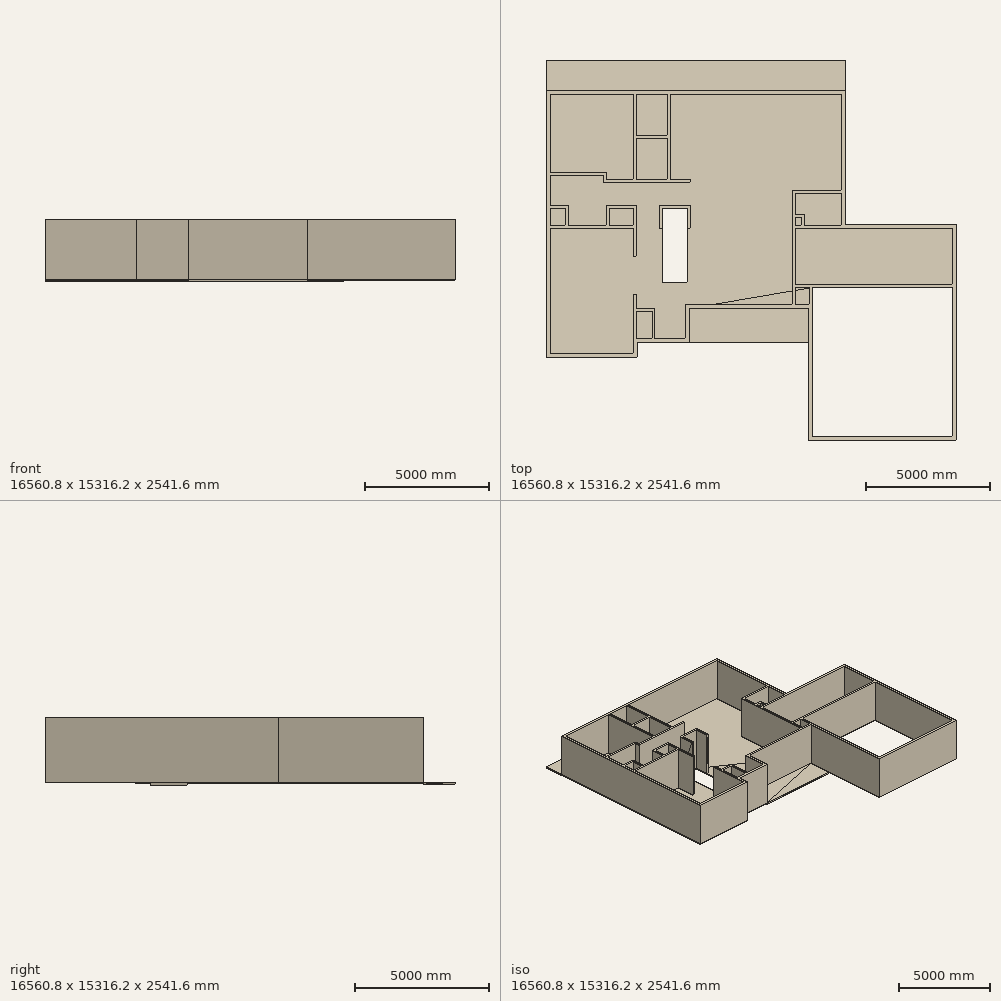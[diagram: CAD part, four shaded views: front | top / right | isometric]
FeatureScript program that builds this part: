
annotation { "Feature Type Name" : "Feature", "Feature Type Description" : "" }
export const myFeature = defineFeature(function(context is Context, id is Id, definition is map)
    precondition{}
    {
        {
            var Q0;
            Q0=qCreatedBy(makeId("Top.planeOp"),FACE);
            cPlane(context, id + "F0", {"entities" : qUnion([Q0]), "cplaneType" : CPlaneType.OFFSET, "offset" : 1.59 * mm, "oppositeDirection" : true, "width" : 152.4 * mm, "height" : 152.4 * mm});
        }
        {
            var Q0;
            Q0=qCreatedBy(makeId("Top.planeOp"),FACE);
            var sketch = newSketch(context, id + "F1", { "sketchPlane" : qUnion([Q0])});
            skLineSegment(sketch, "E0", {"start": v(0, 0) * mm, "end": v(0, 10769.6) * mm});
            skLineSegment(sketch, "E1", {"start": v(0, 10769.6) * mm, "end": v(12065, 10769.6) * mm});
            skLineSegment(sketch, "E2", {"start": v(12065, 10769.6) * mm, "end": v(12065, 5359.4) * mm});
            skLineSegment(sketch, "E3", {"start": v(12065, 5359.4) * mm, "end": v(16560.8, 5359.4) * mm});
            skLineSegment(sketch, "E4", {"start": v(16560.8, 5359.4) * mm, "end": v(16560.8, -3352.8) * mm});
            skLineSegment(sketch, "E5", {"start": v(16560.8, -3352.8) * mm, "end": v(10579.1, -3352.8) * mm});
            skLineSegment(sketch, "E6", {"start": v(10579.1, -3352.8) * mm, "end": v(10579.1, 1955.8) * mm});
            skLineSegment(sketch, "E7", {"start": v(10579.1, 1955.8) * mm, "end": v(5778.5, 1955.8) * mm});
            skLineSegment(sketch, "E8", {"start": v(5778.5, 1955.8) * mm, "end": v(5778.5, 584.2) * mm});
            skLineSegment(sketch, "E9.0", {"start": v(152.4, 152.4) * mm, "end": v(152.4, 10617.2) * mm, "construction": true});
            skLineSegment(sketch, "E9.2", {"start": v(152.4, 10617.2) * mm, "end": v(11912.6, 10617.2) * mm, "construction": true});
            skLineSegment(sketch, "E9.3", {"start": v(5626.1, 2108.2) * mm, "end": v(5626.1, 736.6) * mm, "construction": true});
            skLineSegment(sketch, "E9.4", {"start": v(10731.5, 2108.2) * mm, "end": v(5626.1, 2108.2) * mm, "construction": true});
            skLineSegment(sketch, "E9.5", {"start": v(10731.5, -3200.4) * mm, "end": v(10731.5, 2108.2) * mm, "construction": true});
            skLineSegment(sketch, "E9.6", {"start": v(11912.6, 10617.2) * mm, "end": v(11912.6, 5207) * mm, "construction": true});
            skLineSegment(sketch, "E9.7", {"start": v(11912.6, 5207) * mm, "end": v(16408.4, 5207) * mm, "construction": true});
            skLineSegment(sketch, "E9.8", {"start": v(16408.4, 5207) * mm, "end": v(16408.4, -3200.4) * mm, "construction": true});
            skLineSegment(sketch, "E9.9", {"start": v(16408.4, -3200.4) * mm, "end": v(10731.5, -3200.4) * mm, "construction": true});
            skLineSegment(sketch, "E10", {"start": v(0, 0) * mm, "end": v(0, -114.3) * mm, "construction": true});
            skLineSegment(sketch, "E11.bottom", {"start": v(3505.2, 736.6) * mm, "end": v(3619.5, 736.6) * mm, "construction": true});
            skLineSegment(sketch, "E11.top", {"start": v(3505.2, 2514.6) * mm, "end": v(3619.5, 2514.6) * mm, "construction": true});
            skLineSegment(sketch, "E11.left", {"start": v(3505.2, 736.6) * mm, "end": v(3505.2, 2514.6) * mm, "construction": true});
            skLineSegment(sketch, "E11.right", {"start": v(3619.5, 736.6) * mm, "end": v(3619.5, 2514.6) * mm, "construction": true});
            skLineSegment(sketch, "E12.bottom", {"start": v(3619.5, 4064) * mm, "end": v(3505.2, 4064) * mm, "construction": true});
            skLineSegment(sketch, "E12.top", {"start": v(3619.5, 6121.4) * mm, "end": v(3505.2, 6121.4) * mm, "construction": true});
            skLineSegment(sketch, "E12.left", {"start": v(3619.5, 4064) * mm, "end": v(3619.5, 6121.4) * mm, "construction": true});
            skLineSegment(sketch, "E12.right", {"start": v(3505.2, 4064) * mm, "end": v(3505.2, 6121.4) * mm, "construction": true});
            skLineSegment(sketch, "E13.bottom", {"start": v(3505.2, 6121.4) * mm, "end": v(2425.7, 6121.4) * mm, "construction": true});
            skLineSegment(sketch, "E13.top", {"start": v(3505.2, 6007.1) * mm, "end": v(2425.7, 6007.1) * mm, "construction": true});
            skLineSegment(sketch, "E13.left", {"start": v(3505.2, 6121.4) * mm, "end": v(3505.2, 6007.1) * mm, "construction": true});
            skLineSegment(sketch, "E13.right", {"start": v(2425.7, 6121.4) * mm, "end": v(2425.7, 6007.1) * mm, "construction": true});
            skLineSegment(sketch, "E14.bottom", {"start": v(2425.7, 6007.1) * mm, "end": v(2540, 6007.1) * mm, "construction": true});
            skLineSegment(sketch, "E14.top", {"start": v(2425.7, 5207) * mm, "end": v(2540, 5207) * mm, "construction": true});
            skLineSegment(sketch, "E14.left", {"start": v(2425.7, 6007.1) * mm, "end": v(2425.7, 5207) * mm, "construction": true});
            skLineSegment(sketch, "E14.right", {"start": v(2540, 6007.1) * mm, "end": v(2540, 5207) * mm, "construction": true});
            skLineSegment(sketch, "E15.bottom", {"start": v(2425.7, 5207) * mm, "end": v(152.4, 5207) * mm, "construction": true});
            skLineSegment(sketch, "E15.top", {"start": v(2425.7, 5321.3) * mm, "end": v(152.4, 5321.3) * mm, "construction": true});
            skLineSegment(sketch, "E15.left", {"start": v(2425.7, 5207) * mm, "end": v(2425.7, 5321.3) * mm, "construction": true});
            skLineSegment(sketch, "E15.right", {"start": v(152.4, 5207) * mm, "end": v(152.4, 5321.3) * mm, "construction": true});
            skLineSegment(sketch, "E16.bottom", {"start": v(787.4, 5321.3) * mm, "end": v(901.7, 5321.3) * mm, "construction": true});
            skLineSegment(sketch, "E16.top", {"start": v(787.4, 6007.1) * mm, "end": v(901.7, 6007.1) * mm, "construction": true});
            skLineSegment(sketch, "E16.left", {"start": v(787.4, 5321.3) * mm, "end": v(787.4, 6007.1) * mm, "construction": true});
            skLineSegment(sketch, "E16.right", {"start": v(901.7, 5321.3) * mm, "end": v(901.7, 6007.1) * mm, "construction": true});
            skLineSegment(sketch, "E17.bottom", {"start": v(901.7, 6007.1) * mm, "end": v(152.4, 6007.1) * mm, "construction": true});
            skLineSegment(sketch, "E17.top", {"start": v(901.7, 6121.4) * mm, "end": v(152.4, 6121.4) * mm, "construction": true});
            skLineSegment(sketch, "E17.left", {"start": v(901.7, 6007.1) * mm, "end": v(901.7, 6121.4) * mm, "construction": true});
            skLineSegment(sketch, "E17.right", {"start": v(152.4, 6007.1) * mm, "end": v(152.4, 6121.4) * mm, "construction": true});
            skLineSegment(sketch, "E18.bottom", {"start": v(2413, 7175.5) * mm, "end": v(8356.6, 7175.5) * mm, "construction": true});
            skLineSegment(sketch, "E18.top", {"start": v(2413, 7061.2) * mm, "end": v(8356.6, 7061.2) * mm, "construction": true});
            skLineSegment(sketch, "E18.left", {"start": v(2413, 7175.5) * mm, "end": v(2413, 7061.2) * mm, "construction": true});
            skLineSegment(sketch, "E18.right", {"start": v(8356.6, 7175.5) * mm, "end": v(8356.6, 7061.2) * mm, "construction": true});
            skLineSegment(sketch, "E19.bottom", {"start": v(2540, 5207) * mm, "end": v(3505.2, 5207) * mm, "construction": true});
            skLineSegment(sketch, "E19.top", {"start": v(2540, 5321.3) * mm, "end": v(3505.2, 5321.3) * mm, "construction": true});
            skLineSegment(sketch, "E19.left", {"start": v(2540, 5207) * mm, "end": v(2540, 5321.3) * mm, "construction": true});
            skLineSegment(sketch, "E19.right", {"start": v(3505.2, 5207) * mm, "end": v(3505.2, 5321.3) * mm, "construction": true});
            skLineSegment(sketch, "E20.bottom", {"start": v(4267.2, 736.6) * mm, "end": v(4381.5, 736.6) * mm, "construction": true});
            skLineSegment(sketch, "E20.top", {"start": v(4267.2, 1841.5) * mm, "end": v(4381.5, 1841.5) * mm, "construction": true});
            skLineSegment(sketch, "E20.left", {"start": v(4267.2, 736.6) * mm, "end": v(4267.2, 1841.5) * mm, "construction": true});
            skLineSegment(sketch, "E20.right", {"start": v(4381.5, 736.6) * mm, "end": v(4381.5, 1841.5) * mm, "construction": true});
            skLineSegment(sketch, "E21.bottom", {"start": v(4381.5, 1841.5) * mm, "end": v(3619.5, 1841.5) * mm, "construction": true});
            skLineSegment(sketch, "E21.top", {"start": v(4381.5, 1955.8) * mm, "end": v(3619.5, 1955.8) * mm, "construction": true});
            skLineSegment(sketch, "E21.left", {"start": v(4381.5, 1841.5) * mm, "end": v(4381.5, 1955.8) * mm, "construction": true});
            skLineSegment(sketch, "E21.right", {"start": v(3619.5, 1841.5) * mm, "end": v(3619.5, 1955.8) * mm, "construction": true});
            skLineSegment(sketch, "E22.bottom", {"start": v(8724.9, 2108.2) * mm, "end": v(8839.2, 2108.2) * mm, "construction": true});
            skLineSegment(sketch, "E22.top", {"start": v(8724.9, 3022.6) * mm, "end": v(8839.2, 3022.6) * mm, "construction": true});
            skLineSegment(sketch, "E22.left", {"start": v(8724.9, 2108.2) * mm, "end": v(8724.9, 3022.6) * mm, "construction": true});
            skLineSegment(sketch, "E22.right", {"start": v(8839.2, 2108.2) * mm, "end": v(8839.2, 3022.6) * mm, "construction": true});
            skLineSegment(sketch, "E23.bottom", {"start": v(10731.5, 2108.2) * mm, "end": v(10617.2, 2108.2) * mm, "construction": true});
            skLineSegment(sketch, "E23.top", {"start": v(10731.5, 2806.7) * mm, "end": v(10617.2, 2806.7) * mm, "construction": true});
            skLineSegment(sketch, "E23.left", {"start": v(10731.5, 2108.2) * mm, "end": v(10731.5, 2806.7) * mm, "construction": true});
            skLineSegment(sketch, "E23.right", {"start": v(10617.2, 2108.2) * mm, "end": v(10617.2, 2806.7) * mm, "construction": true});
            skLineSegment(sketch, "E24.bottom", {"start": v(10617.2, 2806.7) * mm, "end": v(16408.4, 2806.7) * mm, "construction": true});
            skLineSegment(sketch, "E24.top", {"start": v(10617.2, 2921) * mm, "end": v(16408.4, 2921) * mm, "construction": true});
            skLineSegment(sketch, "E24.left", {"start": v(10617.2, 2806.7) * mm, "end": v(10617.2, 2921) * mm, "construction": true});
            skLineSegment(sketch, "E24.right", {"start": v(16408.4, 2806.7) * mm, "end": v(16408.4, 2921) * mm, "construction": true});
            skLineSegment(sketch, "E25.bottom", {"start": v(2413, 7061.2) * mm, "end": v(2298.7, 7061.2) * mm, "construction": true});
            skLineSegment(sketch, "E25.top", {"start": v(2413, 7327.9) * mm, "end": v(2298.7, 7327.9) * mm, "construction": true});
            skLineSegment(sketch, "E25.left", {"start": v(2413, 7061.2) * mm, "end": v(2413, 7327.9) * mm, "construction": true});
            skLineSegment(sketch, "E25.right", {"start": v(2298.7, 7061.2) * mm, "end": v(2298.7, 7327.9) * mm, "construction": true});
            skLineSegment(sketch, "E26.bottom", {"start": v(2413, 7327.9) * mm, "end": v(152.4, 7327.9) * mm, "construction": true});
            skLineSegment(sketch, "E26.top", {"start": v(2413, 7442.2) * mm, "end": v(152.4, 7442.2) * mm, "construction": true});
            skLineSegment(sketch, "E26.left", {"start": v(2413, 7327.9) * mm, "end": v(2413, 7442.2) * mm, "construction": true});
            skLineSegment(sketch, "E26.right", {"start": v(152.4, 7327.9) * mm, "end": v(152.4, 7442.2) * mm, "construction": true});
            skLineSegment(sketch, "E27.bottom", {"start": v(3505.2, 7175.5) * mm, "end": v(3619.5, 7175.5) * mm, "construction": true});
            skLineSegment(sketch, "E27.top", {"start": v(3505.2, 10617.2) * mm, "end": v(3619.5, 10617.2) * mm, "construction": true});
            skLineSegment(sketch, "E27.left", {"start": v(3505.2, 7175.5) * mm, "end": v(3505.2, 10617.2) * mm, "construction": true});
            skLineSegment(sketch, "E27.right", {"start": v(3619.5, 7175.5) * mm, "end": v(3619.5, 10617.2) * mm, "construction": true});
            skLineSegment(sketch, "E28.bottom", {"start": v(4889.5, 10617.2) * mm, "end": v(5003.8, 10617.2) * mm, "construction": true});
            skLineSegment(sketch, "E28.top", {"start": v(4889.5, 7175.5) * mm, "end": v(5003.8, 7175.5) * mm, "construction": true});
            skLineSegment(sketch, "E28.left", {"start": v(4889.5, 10617.2) * mm, "end": v(4889.5, 7175.5) * mm, "construction": true});
            skLineSegment(sketch, "E28.right", {"start": v(5003.8, 10617.2) * mm, "end": v(5003.8, 7175.5) * mm, "construction": true});
            skLineSegment(sketch, "E29.bottom", {"start": v(3619.5, 8940.8) * mm, "end": v(4889.5, 8940.8) * mm, "construction": true});
            skLineSegment(sketch, "E29.top", {"start": v(3619.5, 8826.5) * mm, "end": v(4889.5, 8826.5) * mm, "construction": true});
            skLineSegment(sketch, "E29.left", {"start": v(3619.5, 8940.8) * mm, "end": v(3619.5, 8826.5) * mm, "construction": true});
            skLineSegment(sketch, "E29.right", {"start": v(4889.5, 8940.8) * mm, "end": v(4889.5, 8826.5) * mm, "construction": true});
            skLineSegment(sketch, "E30.bottom", {"start": v(4559.3, 5207) * mm, "end": v(4673.6, 5207) * mm, "construction": true});
            skLineSegment(sketch, "E30.top", {"start": v(4559.3, 6121.4) * mm, "end": v(4673.6, 6121.4) * mm, "construction": true});
            skLineSegment(sketch, "E30.left", {"start": v(4559.3, 5207) * mm, "end": v(4559.3, 6121.4) * mm, "construction": true});
            skLineSegment(sketch, "E30.right", {"start": v(4673.6, 5207) * mm, "end": v(4673.6, 6121.4) * mm, "construction": true});
            skLineSegment(sketch, "E31.bottom", {"start": v(4673.6, 6121.4) * mm, "end": v(5715, 6121.4) * mm, "construction": true});
            skLineSegment(sketch, "E31.top", {"start": v(4673.6, 6007.1) * mm, "end": v(5715, 6007.1) * mm, "construction": true});
            skLineSegment(sketch, "E31.left", {"start": v(4673.6, 6121.4) * mm, "end": v(4673.6, 6007.1) * mm, "construction": true});
            skLineSegment(sketch, "E31.right", {"start": v(5715, 6121.4) * mm, "end": v(5715, 6007.1) * mm, "construction": true});
            skLineSegment(sketch, "E32.bottom", {"start": v(5715, 6121.4) * mm, "end": v(5829.3, 6121.4) * mm, "construction": true});
            skLineSegment(sketch, "E32.top", {"start": v(5715, 5321.3) * mm, "end": v(5829.3, 5321.3) * mm, "construction": true});
            skLineSegment(sketch, "E32.left", {"start": v(5715, 6121.4) * mm, "end": v(5715, 5321.3) * mm, "construction": true});
            skLineSegment(sketch, "E32.right", {"start": v(5829.3, 6121.4) * mm, "end": v(5829.3, 5321.3) * mm, "construction": true});
            skLineSegment(sketch, "E33.bottom", {"start": v(5715, 5321.3) * mm, "end": v(11912.6, 5321.3) * mm, "construction": true});
            skLineSegment(sketch, "E33.top", {"start": v(5715, 5207) * mm, "end": v(11912.6, 5207) * mm, "construction": true});
            skLineSegment(sketch, "E33.left", {"start": v(5715, 5321.3) * mm, "end": v(5715, 5207) * mm, "construction": true});
            skLineSegment(sketch, "E33.right", {"start": v(11912.6, 5321.3) * mm, "end": v(11912.6, 5207) * mm, "construction": true});
            skLineSegment(sketch, "E34.bottom", {"start": v(11912.6, 6731) * mm, "end": v(9550.4, 6731) * mm, "construction": true});
            skLineSegment(sketch, "E34.top", {"start": v(11912.6, 6616.7) * mm, "end": v(9550.4, 6616.7) * mm, "construction": true});
            skLineSegment(sketch, "E34.left", {"start": v(11912.6, 6731) * mm, "end": v(11912.6, 6616.7) * mm, "construction": true});
            skLineSegment(sketch, "E34.right", {"start": v(9550.4, 6731) * mm, "end": v(9550.4, 6616.7) * mm, "construction": true});
            skLineSegment(sketch, "E35.bottom", {"start": v(9550.4, 6731) * mm, "end": v(9436.1, 6731) * mm, "construction": true});
            skLineSegment(sketch, "E35.top", {"start": v(9550.4, 5321.3) * mm, "end": v(9436.1, 5321.3) * mm, "construction": true});
            skLineSegment(sketch, "E35.left", {"start": v(9550.4, 6731) * mm, "end": v(9550.4, 5321.3) * mm, "construction": true});
            skLineSegment(sketch, "E35.right", {"start": v(9436.1, 6731) * mm, "end": v(9436.1, 5321.3) * mm, "construction": true});
            skLineSegment(sketch, "E36.bottom", {"start": v(8724.9, 5207) * mm, "end": v(8839.2, 5207) * mm, "construction": true});
            skLineSegment(sketch, "E36.top", {"start": v(8724.9, 3937) * mm, "end": v(8839.2, 3937) * mm, "construction": true});
            skLineSegment(sketch, "E36.left", {"start": v(8724.9, 5207) * mm, "end": v(8724.9, 3937) * mm, "construction": true});
            skLineSegment(sketch, "E36.right", {"start": v(8839.2, 5207) * mm, "end": v(8839.2, 3937) * mm, "construction": true});
            skLineSegment(sketch, "E37.bottom", {"start": v(5829.3, 6007.1) * mm, "end": v(9436.1, 6007.1) * mm, "construction": true});
            skLineSegment(sketch, "E37.top", {"start": v(5829.3, 6121.4) * mm, "end": v(9436.1, 6121.4) * mm, "construction": true});
            skLineSegment(sketch, "E37.left", {"start": v(5829.3, 6007.1) * mm, "end": v(5829.3, 6121.4) * mm, "construction": true});
            skLineSegment(sketch, "E37.right", {"start": v(9436.1, 6007.1) * mm, "end": v(9436.1, 6121.4) * mm, "construction": true});
            skLineSegment(sketch, "E38", {"start": v(3619.5, 736.6) * mm, "end": v(3619.5, 1841.5) * mm});
            skLineSegment(sketch, "E39", {"start": v(4267.2, 1841.5) * mm, "end": v(4267.2, 736.6) * mm});
            skLineSegment(sketch, "E40", {"start": v(3619.5, 1841.5) * mm, "end": v(4267.2, 1841.5) * mm});
            skLineSegment(sketch, "E41", {"start": v(4267.2, 736.6) * mm, "end": v(3619.5, 736.6) * mm});
            skLineSegment(sketch, "E42", {"start": v(152.4, 6007.1) * mm, "end": v(787.4, 6007.1) * mm});
            skLineSegment(sketch, "E43", {"start": v(787.4, 6007.1) * mm, "end": v(787.4, 5321.3) * mm});
            skLineSegment(sketch, "E44", {"start": v(787.4, 5321.3) * mm, "end": v(152.4, 5321.3) * mm});
            skLineSegment(sketch, "E45", {"start": v(152.4, 6007.1) * mm, "end": v(152.4, 5321.3) * mm});
            skLineSegment(sketch, "E46", {"start": v(2540, 5321.3) * mm, "end": v(2540, 6007.1) * mm});
            skLineSegment(sketch, "E47", {"start": v(3505.2, 6007.1) * mm, "end": v(3505.2, 5321.3) * mm});
            skLineSegment(sketch, "E48", {"start": v(2540, 6007.1) * mm, "end": v(3505.2, 6007.1) * mm});
            skLineSegment(sketch, "E49", {"start": v(3505.2, 5321.3) * mm, "end": v(2540, 5321.3) * mm});
            skLineSegment(sketch, "E50", {"start": v(3619.5, 8826.5) * mm, "end": v(4889.5, 8826.5) * mm});
            skLineSegment(sketch, "E51", {"start": v(4889.5, 7175.5) * mm, "end": v(3619.5, 7175.5) * mm});
            skLineSegment(sketch, "E52", {"start": v(4889.5, 7175.5) * mm, "end": v(4889.5, 8826.5) * mm});
            skLineSegment(sketch, "E53", {"start": v(3619.5, 8826.5) * mm, "end": v(3619.5, 7175.5) * mm});
            skLineSegment(sketch, "E54", {"start": v(3619.5, 8940.8) * mm, "end": v(4889.5, 8940.8) * mm});
            skLineSegment(sketch, "E55", {"start": v(4889.5, 10617.2) * mm, "end": v(3619.5, 10617.2) * mm});
            skLineSegment(sketch, "E56", {"start": v(4889.5, 8940.8) * mm, "end": v(4889.5, 10617.2) * mm});
            skLineSegment(sketch, "E57", {"start": v(3619.5, 10617.2) * mm, "end": v(3619.5, 8940.8) * mm});
            skLineSegment(sketch, "E58", {"start": v(9436.1, 5321.3) * mm, "end": v(9436.1, 6007.1) * mm});
            skLineSegment(sketch, "E59", {"start": v(9436.1, 5321.3) * mm, "end": v(5829.3, 5321.3) * mm});
            skLineSegment(sketch, "E60", {"start": v(5829.3, 5321.3) * mm, "end": v(5829.3, 6007.1) * mm});
            skLineSegment(sketch, "E61", {"start": v(9436.1, 6007.1) * mm, "end": v(5829.3, 6007.1) * mm});
            skLineSegment(sketch, "E62", {"start": v(10731.5, 2806.7) * mm, "end": v(10731.5, -3200.4) * mm});
            skLineSegment(sketch, "E63", {"start": v(16408.4, -3200.4) * mm, "end": v(16408.4, 2806.7) * mm});
            skLineSegment(sketch, "E64", {"start": v(16408.4, -3200.4) * mm, "end": v(10731.5, -3200.4) * mm});
            skLineSegment(sketch, "E65", {"start": v(10731.5, 2806.7) * mm, "end": v(16408.4, 2806.7) * mm});
            skLineSegment(sketch, "E66", {"start": v(152.4, 5207) * mm, "end": v(152.4, 152.4) * mm});
            skLineSegment(sketch, "E67", {"start": v(152.4, 152.4) * mm, "end": v(3505.2, 152.4) * mm});
            skLineSegment(sketch, "E68", {"start": v(3505.2, 736.6) * mm, "end": v(3505.2, 2514.6) * mm});
            skLineSegment(sketch, "E69", {"start": v(3505.2, 2514.6) * mm, "end": v(3619.5, 2514.6) * mm});
            skLineSegment(sketch, "E70", {"start": v(3619.5, 1955.8) * mm, "end": v(3619.5, 2514.6) * mm});
            skLineSegment(sketch, "E71", {"start": v(3619.5, 1955.8) * mm, "end": v(4381.5, 1955.8) * mm});
            skLineSegment(sketch, "E72", {"start": v(4381.5, 736.6) * mm, "end": v(4381.5, 1955.8) * mm});
            skLineSegment(sketch, "E73", {"start": v(4381.5, 736.6) * mm, "end": v(5626.1, 736.6) * mm});
            skLineSegment(sketch, "E74", {"start": v(5626.1, 736.6) * mm, "end": v(5626.1, 2108.2) * mm});
            skLineSegment(sketch, "E75", {"start": v(5626.1, 2108.2) * mm, "end": v(8724.9, 2108.2) * mm});
            skLineSegment(sketch, "E76", {"start": v(8724.9, 3022.6) * mm, "end": v(8724.9, 2108.2) * mm});
            skLineSegment(sketch, "E77", {"start": v(8724.9, 3022.6) * mm, "end": v(8839.2, 3022.6) * mm});
            skLineSegment(sketch, "E78", {"start": v(8839.2, 2108.2) * mm, "end": v(8839.2, 3022.6) * mm});
            skLineSegment(sketch, "E79", {"start": v(8839.2, 2108.2) * mm, "end": v(10617.2, 2108.2) * mm});
            skLineSegment(sketch, "E80", {"start": v(10617.2, 2921) * mm, "end": v(10617.2, 2108.2) * mm});
            skLineSegment(sketch, "E81", {"start": v(10617.2, 2921) * mm, "end": v(16408.4, 2921) * mm});
            skLineSegment(sketch, "E82", {"start": v(16408.4, 5207) * mm, "end": v(16408.4, 2921) * mm});
            skLineSegment(sketch, "E83", {"start": v(16408.4, 5207) * mm, "end": v(8839.2, 5207) * mm});
            skLineSegment(sketch, "E84", {"start": v(8839.2, 3937) * mm, "end": v(8839.2, 5207) * mm});
            skLineSegment(sketch, "E85", {"start": v(8839.2, 3937) * mm, "end": v(8724.9, 3937) * mm});
            skLineSegment(sketch, "E86", {"start": v(8724.9, 5207) * mm, "end": v(8724.9, 3937) * mm});
            skLineSegment(sketch, "E87", {"start": v(8724.9, 5207) * mm, "end": v(5715, 5207) * mm});
            skLineSegment(sketch, "E88", {"start": v(5715, 6007.1) * mm, "end": v(4673.6, 6007.1) * mm});
            skLineSegment(sketch, "E89", {"start": v(5715, 6007.1) * mm, "end": v(5715, 5207) * mm});
            skLineSegment(sketch, "E90", {"start": v(4673.6, 5207) * mm, "end": v(4673.6, 6007.1) * mm});
            skLineSegment(sketch, "E91", {"start": v(4673.6, 5207) * mm, "end": v(4559.3, 5207) * mm});
            skLineSegment(sketch, "E92", {"start": v(4559.3, 6121.4) * mm, "end": v(4559.3, 5207) * mm});
            skLineSegment(sketch, "E93", {"start": v(4559.3, 6121.4) * mm, "end": v(9436.1, 6121.4) * mm});
            skLineSegment(sketch, "E94", {"start": v(9436.1, 6731) * mm, "end": v(9436.1, 6121.4) * mm});
            skLineSegment(sketch, "E95", {"start": v(9436.1, 6731) * mm, "end": v(11912.6, 6731) * mm});
            skLineSegment(sketch, "E96", {"start": v(11912.6, 6731) * mm, "end": v(11912.6, 10617.2) * mm});
            skLineSegment(sketch, "E97", {"start": v(11912.6, 10617.2) * mm, "end": v(5003.8, 10617.2) * mm});
            skLineSegment(sketch, "E98", {"start": v(5003.8, 7175.5) * mm, "end": v(5003.8, 10617.2) * mm});
            skLineSegment(sketch, "E99", {"start": v(8356.6, 7175.5) * mm, "end": v(5003.8, 7175.5) * mm});
            skLineSegment(sketch, "E100", {"start": v(8356.6, 7175.5) * mm, "end": v(8356.6, 7061.2) * mm});
            skLineSegment(sketch, "E101", {"start": v(2298.7, 7061.2) * mm, "end": v(8356.6, 7061.2) * mm});
            skLineSegment(sketch, "E102", {"start": v(2298.7, 7061.2) * mm, "end": v(2298.7, 7327.9) * mm});
            skLineSegment(sketch, "E103", {"start": v(152.4, 6121.4) * mm, "end": v(152.4, 7327.9) * mm});
            skLineSegment(sketch, "E104", {"start": v(2298.7, 7327.9) * mm, "end": v(152.4, 7327.9) * mm});
            skLineSegment(sketch, "E105", {"start": v(152.4, 6121.4) * mm, "end": v(901.7, 6121.4) * mm});
            skLineSegment(sketch, "E106", {"start": v(901.7, 5321.3) * mm, "end": v(901.7, 6121.4) * mm});
            skLineSegment(sketch, "E107", {"start": v(2425.7, 5321.3) * mm, "end": v(901.7, 5321.3) * mm});
            skLineSegment(sketch, "E108", {"start": v(2425.7, 6121.4) * mm, "end": v(2425.7, 5321.3) * mm});
            skLineSegment(sketch, "E109", {"start": v(2425.7, 6121.4) * mm, "end": v(3619.5, 6121.4) * mm});
            skLineSegment(sketch, "E110", {"start": v(3619.5, 4064) * mm, "end": v(3505.2, 4064) * mm});
            skLineSegment(sketch, "E111", {"start": v(3619.5, 4064) * mm, "end": v(3619.5, 6121.4) * mm});
            skLineSegment(sketch, "E112", {"start": v(3505.2, 4064) * mm, "end": v(3505.2, 5207) * mm});
            skLineSegment(sketch, "E113", {"start": v(152.4, 5207) * mm, "end": v(3505.2, 5207) * mm});
            skLineSegment(sketch, "E114", {"start": v(152.4, 10617.2) * mm, "end": v(152.4, 7442.2) * mm});
            skLineSegment(sketch, "E115", {"start": v(2413, 7442.2) * mm, "end": v(152.4, 7442.2) * mm});
            skLineSegment(sketch, "E116", {"start": v(2413, 7175.5) * mm, "end": v(2413, 7442.2) * mm});
            skLineSegment(sketch, "E117", {"start": v(3505.2, 7175.5) * mm, "end": v(2413, 7175.5) * mm});
            skLineSegment(sketch, "E118", {"start": v(3505.2, 7175.5) * mm, "end": v(3505.2, 10617.2) * mm});
            skLineSegment(sketch, "E119", {"start": v(3505.2, 10617.2) * mm, "end": v(152.4, 10617.2) * mm});
            skLineSegment(sketch, "E120.bottom", {"start": v(9550.4, 5753.1) * mm, "end": v(10299.7, 5753.1) * mm, "construction": true});
            skLineSegment(sketch, "E120.top", {"start": v(9550.4, 5638.8) * mm, "end": v(10299.7, 5638.8) * mm, "construction": true});
            skLineSegment(sketch, "E120.left", {"start": v(9550.4, 5753.1) * mm, "end": v(9550.4, 5638.8) * mm, "construction": true});
            skLineSegment(sketch, "E120.right", {"start": v(10299.7, 5753.1) * mm, "end": v(10299.7, 5638.8) * mm, "construction": true});
            skLineSegment(sketch, "E121.bottom", {"start": v(10299.7, 5753.1) * mm, "end": v(10414, 5753.1) * mm, "construction": true});
            skLineSegment(sketch, "E121.top", {"start": v(10299.7, 5321.3) * mm, "end": v(10414, 5321.3) * mm, "construction": true});
            skLineSegment(sketch, "E121.left", {"start": v(10299.7, 5753.1) * mm, "end": v(10299.7, 5321.3) * mm, "construction": true});
            skLineSegment(sketch, "E121.right", {"start": v(10414, 5753.1) * mm, "end": v(10414, 5321.3) * mm, "construction": true});
            skLineSegment(sketch, "E122", {"start": v(9550.4, 6616.7) * mm, "end": v(9550.4, 5753.1) * mm});
            skLineSegment(sketch, "E123", {"start": v(10414, 5753.1) * mm, "end": v(9550.4, 5753.1) * mm});
            skLineSegment(sketch, "E124", {"start": v(10414, 5321.3) * mm, "end": v(10414, 5753.1) * mm});
            skLineSegment(sketch, "E125", {"start": v(10414, 5321.3) * mm, "end": v(11912.6, 5321.3) * mm});
            skLineSegment(sketch, "E126", {"start": v(11912.6, 5321.3) * mm, "end": v(11912.6, 6616.7) * mm});
            skLineSegment(sketch, "E127", {"start": v(9550.4, 6616.7) * mm, "end": v(11912.6, 6616.7) * mm});
            skLineSegment(sketch, "E128", {"start": v(9550.4, 5321.3) * mm, "end": v(9550.4, 5638.8) * mm});
            skLineSegment(sketch, "E129", {"start": v(10299.7, 5638.8) * mm, "end": v(10299.7, 5321.3) * mm});
            skLineSegment(sketch, "E130", {"start": v(10299.7, 5638.8) * mm, "end": v(9550.4, 5638.8) * mm});
            skLineSegment(sketch, "E131", {"start": v(9550.4, 5321.3) * mm, "end": v(10299.7, 5321.3) * mm});
            skLineSegment(sketch, "E132", {"start": v(3505.2, 152.4) * mm, "end": v(3505.2, 736.6) * mm});
            skLineSegment(sketch, "E133", {"start": v(0, 0) * mm, "end": v(3657.6, 0) * mm});
            skLineSegment(sketch, "E134", {"start": v(3657.6, 0) * mm, "end": v(3657.6, 584.2) * mm});
            skLineSegment(sketch, "E135", {"start": v(5778.5, 584.2) * mm, "end": v(3657.6, 584.2) * mm});
            skLineSegment(sketch, "E136", {"start": v(0, -114.3) * mm, "end": v(0, -266.7) * mm, "construction": true});
            skLineSegment(sketch, "E137", {"start": v(3505.2, 152.4) * mm, "end": v(3505.2, 0) * mm, "construction": true});
            skLineSegment(sketch, "E138", {"start": v(3505.2, 152.4) * mm, "end": v(3657.6, 152.4) * mm, "construction": true});
            skLineSegment(sketch, "E139", {"start": v(5626.1, 736.6) * mm, "end": v(5626.1, 584.2) * mm, "construction": true});
            skSolve(sketch);
        }
        {
            var Q0;
            Q0 = qSketchRegion(id + "F1", true);
            var Q1;
            Q1 = qConstructionFilter(qBodyType(qCreatedBy(id + "F1" ,EDGE), BodyType.WIRE), ConstructionObject.NO);
            extrude(context, id + "F2", {"entities" : qUnion([Q0]), "surfaceEntities" : qUnion([Q1]), "depth" : 2438.4 * mm, "offsetDistance" : 25.4 * mm});
        }
        {
            var Q0;
            Q0=qCreatedBy(id+"F0.planeOp",FACE);
            var sketch = newSketch(context, id + "F3", { "sketchPlane" : qUnion([Q0])});
            skLineSegment(sketch, "E140", {"start": v(0, 0) * mm, "end": v(0, 10769.6) * mm});
            skLineSegment(sketch, "E141", {"start": v(0, 10769.6) * mm, "end": v(12065, 10769.6) * mm});
            skLineSegment(sketch, "E142", {"start": v(12065, 10769.6) * mm, "end": v(12065, 5359.4) * mm});
            skLineSegment(sketch, "E143", {"start": v(12065, 5359.4) * mm, "end": v(16560.8, 5359.4) * mm});
            skLineSegment(sketch, "E144", {"start": v(16560.8, 5359.4) * mm, "end": v(16560.8, 2806.7) * mm});
            skLineSegment(sketch, "E145", {"start": v(16560.8, 2806.7) * mm, "end": v(10731.5, 2806.7) * mm});
            skLineSegment(sketch, "E146", {"start": v(10731.5, 2806.7) * mm, "end": v(10731.5, 1955.8) * mm});
            skLineSegment(sketch, "E147", {"start": v(10731.5, 1955.8) * mm, "end": v(5778.5, 1955.8) * mm});
            skLineSegment(sketch, "E148", {"start": v(5778.5, 1955.8) * mm, "end": v(5778.5, 584.2) * mm});
            skLineSegment(sketch, "E149", {"start": v(3657.6, 0) * mm, "end": v(0, 0) * mm});
            skLineSegment(sketch, "E150.bottom", {"start": v(4673.6, 3022.6) * mm, "end": v(5715, 3022.6) * mm});
            skLineSegment(sketch, "E150.top", {"start": v(4673.6, 6007.1) * mm, "end": v(5715, 6007.1) * mm});
            skLineSegment(sketch, "E150.left", {"start": v(4673.6, 3022.6) * mm, "end": v(4673.6, 6007.1) * mm});
            skLineSegment(sketch, "E150.right", {"start": v(5715, 3022.6) * mm, "end": v(5715, 6007.1) * mm});
            skLineSegment(sketch, "E151", {"start": v(3657.6, 0) * mm, "end": v(3657.6, 584.2) * mm});
            skLineSegment(sketch, "E152", {"start": v(3657.6, 584.2) * mm, "end": v(5778.5, 584.2) * mm});
            skSolve(sketch);
        }
        {
            var Q0;
            Q0 = qSketchRegion(id + "F3", true);
            extrude(context, id + "F4", {"entities" : qUnion([Q0]), "oppositeDirection" : true, "depth" : 31.75 * mm, "offsetDistance" : 25.4 * mm});
        }
        {
            var Q0;
            Q0=qCreatedBy(id+"F0.planeOp",FACE);
            var sketch = newSketch(context, id + "F5", { "sketchPlane" : qUnion([Q0])});
            skLineSegment(sketch, "E153.bottom", {"start": v(0, 11963.4) * mm, "end": v(12065, 11963.4) * mm});
            skLineSegment(sketch, "E153.top", {"start": v(0, 10769.6) * mm, "end": v(12065, 10769.6) * mm});
            skLineSegment(sketch, "E153.left", {"start": v(0, 11963.4) * mm, "end": v(0, 10769.6) * mm});
            skLineSegment(sketch, "E153.right", {"start": v(12065, 11963.4) * mm, "end": v(12065, 10769.6) * mm});
            skSolve(sketch);
        }
        {
            var Q0;
            Q0 = qSketchRegion(id + "F5", true);
            extrude(context, id + "F6", {"entities" : qUnion([Q0]), "oppositeDirection" : true, "depth" : 76.2 * mm, "offsetDistance" : 25.4 * mm});
        }
        {
            var Q0;
            Q0=qCreatedBy(id+"F0.planeOp",FACE);
            var sketch = newSketch(context, id + "F7", { "sketchPlane" : qUnion([Q0])});
            skLineSegment(sketch, "E154.bottom", {"start": v(5778.5, 584.2) * mm, "end": v(10579.1, 584.2) * mm});
            skLineSegment(sketch, "E154.top", {"start": v(5778.5, 1955.8) * mm, "end": v(10579.1, 1955.8) * mm});
            skLineSegment(sketch, "E154.left", {"start": v(5778.5, 584.2) * mm, "end": v(5778.5, 1955.8) * mm});
            skLineSegment(sketch, "E154.right", {"start": v(10579.1, 584.2) * mm, "end": v(10579.1, 1955.8) * mm});
            skSolve(sketch);
        }
        {
            var Q0;
            Q0 = qSketchRegion(id + "F7", true);
            extrude(context, id + "F8", {"entities" : qUnion([Q0]), "oppositeDirection" : true, "depth" : 101.6 * mm, "offsetDistance" : 25.4 * mm});
        }
        {
            var Q0;
            Q0=qCreatedBy(makeId("Top.planeOp"),FACE);
            var sketch = newSketch(context, id + "F9", { "sketchPlane" : qUnion([Q0])});
            skLineSegment(sketch, "E155.bottom", {"start": v(10045.7, 2108.2) * mm, "end": v(5829.3, 2108.2) * mm});
            skLineSegment(sketch, "E155.top", {"start": v(10045.7, 7175.5) * mm, "end": v(5829.3, 7175.5) * mm});
            skLineSegment(sketch, "E155.left", {"start": v(10045.7, 2108.2) * mm, "end": v(10045.7, 7175.5) * mm});
            skLineSegment(sketch, "E155.right", {"start": v(5829.3, 2108.2) * mm, "end": v(5829.3, 7175.5) * mm});
            skSolve(sketch);
        }
        {
            var Q0;
            Q0 = qSketchRegion(id + "F9", true);
            extrude(context, id + "F10", {"entities" : qUnion([Q0]), "operationType" : NewBodyOperationType.REMOVE, "endBound" : BoundingType.THROUGH_ALL, "depth" : 25.4 * mm, "offsetDistance" : 25.4 * mm});
        }
        {
            var Q0;
            Q0=qCreatedBy(makeId("Top.planeOp"),FACE);
            var sketch = newSketch(context, id + "F11", { "sketchPlane" : qUnion([Q0])});
            skLineSegment(sketch, "E156.bottom", {"start": v(9931.4, 6731) * mm, "end": v(10045.7, 6731) * mm});
            skLineSegment(sketch, "E156.top", {"start": v(9931.4, 2108.2) * mm, "end": v(10045.7, 2108.2) * mm});
            skLineSegment(sketch, "E156.left", {"start": v(9931.4, 6731) * mm, "end": v(9931.4, 2108.2) * mm});
            skLineSegment(sketch, "E156.right", {"start": v(10045.7, 6731) * mm, "end": v(10045.7, 2108.2) * mm});
            skLineSegment(sketch, "E157.bottom", {"start": v(10045.7, 2806.7) * mm, "end": v(10617.2, 2806.7) * mm});
            skLineSegment(sketch, "E157.top", {"start": v(10045.7, 2921) * mm, "end": v(10617.2, 2921) * mm});
            skLineSegment(sketch, "E157.left", {"start": v(10045.7, 2806.7) * mm, "end": v(10045.7, 2921) * mm});
            skLineSegment(sketch, "E157.right", {"start": v(10617.2, 2806.7) * mm, "end": v(10617.2, 2921) * mm});
            skSolve(sketch);
        }
        {
            var Q0;
            Q0 = qSketchRegion(id + "F11", true);
            extrude(context, id + "F12", {"entities" : qUnion([Q0]), "operationType" : NewBodyOperationType.ADD, "depth" : 2438.4 * mm, "offsetDistance" : 25.4 * mm});
        }
    });
